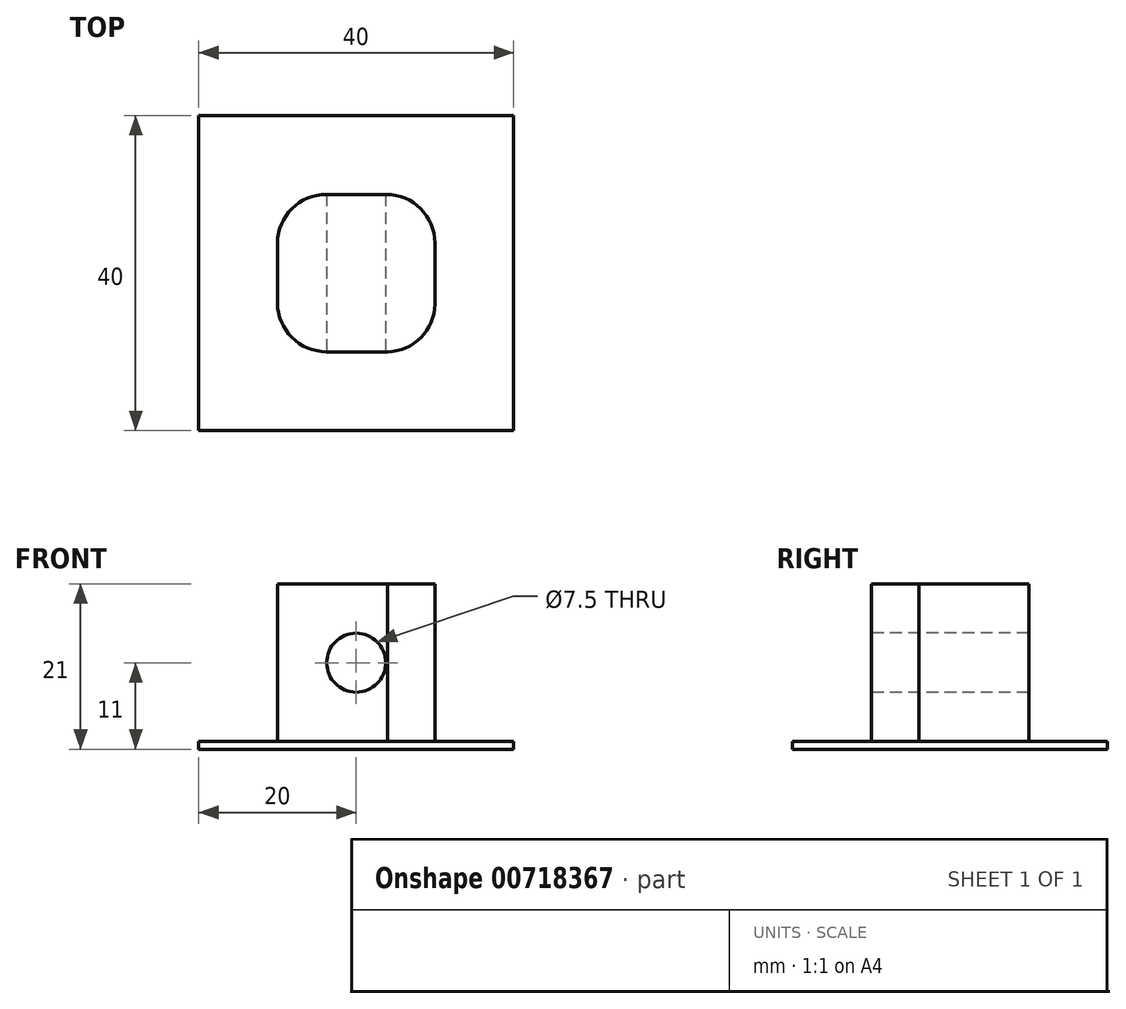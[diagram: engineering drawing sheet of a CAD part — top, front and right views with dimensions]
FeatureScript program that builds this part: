
annotation { "Feature Type Name" : "Feature", "Feature Type Description" : "" }
export const myFeature = defineFeature(function(context is Context, id is Id, definition is map)
    precondition{}
    {
        {
            var Q0;
            Q0=qCreatedBy(makeId("Top.planeOp"),FACE);
            var sketch = newSketch(context, id + "F0", { "sketchPlane" : qUnion([Q0])});
            skLineSegment(sketch, "E0.bottom", {"start": v(20, -20) * mm, "end": v(-20, -20) * mm});
            skLineSegment(sketch, "E0.top", {"start": v(20, 20) * mm, "end": v(-20, 20) * mm});
            skLineSegment(sketch, "E0.left", {"start": v(20, -20) * mm, "end": v(20, 20) * mm});
            skLineSegment(sketch, "E0.right", {"start": v(-20, -20) * mm, "end": v(-20, 20) * mm});
            skPoint(sketch, "E0.middle", {"position": v(0, 0) * mm});
            skSolve(sketch);
        }
        {
            var Q0;
            Q0=makeQuery(id+"F0.imprint","IMPRINT",FACE,{"disambiguationData":[TD([[makeQuery(id+"F0.imprint","IMPRINT",EDGE,{"derivedFrom":sQuery(id+"F0.wireOp",EDGE,"E0.bottom")}),-1.0]])]});
            extrude(context, id + "F1", {"entities" : qUnion([Q0]), "depth" : 1 * mm, "offsetDistance" : 25 * mm});
        }
        {
            var Q0;
            Q0=makeQuery(id+"F1.opExtrude","CAP_FACE",FACE,{"disambiguationData":[OSD([sQuery(id+"F0.wireOp",EDGE,"E0.bottom"),sQuery(id+"F0.wireOp",EDGE,"E0.top"),sQuery(id+"F0.wireOp",EDGE,"E0.left"),sQuery(id+"F0.wireOp",EDGE,"E0.right")])],"isStart":false});
            var sketch = newSketch(context, id + "F2", { "sketchPlane" : qUnion([Q0])});
            skLineSegment(sketch, "E1.bottom", {"start": v(10, -10) * mm, "end": v(-10, -10) * mm});
            skLineSegment(sketch, "E1.top", {"start": v(10, 10) * mm, "end": v(-10, 10) * mm});
            skLineSegment(sketch, "E1.left", {"start": v(10, -10) * mm, "end": v(10, 10) * mm});
            skLineSegment(sketch, "E1.right", {"start": v(-10, -10) * mm, "end": v(-10, 10) * mm});
            skPoint(sketch, "E1.middle", {"position": v(0, 0) * mm});
            skSolve(sketch);
        }
        {
            var Q0;
            Q0=makeQuery(id+"F2.imprint","IMPRINT",FACE,{"disambiguationData":[TD([[makeQuery(id+"F2.imprint","IMPRINT",EDGE,{"derivedFrom":sQuery(id+"F2.wireOp",EDGE,"E1.bottom")}),-1.0]])]});
            extrude(context, id + "F3", {"entities" : qUnion([Q0]), "operationType" : NewBodyOperationType.ADD, "depth" : 20 * mm, "offsetDistance" : 25 * mm});
        }
        {
            var Q0;
            Q0=makeQuery(id+"F3.opExtrude","SWEPT_FACE",FACE,{"disambiguationData":[OSD([sQuery(id+"F2.wireOp",EDGE,"E1.bottom")])]});
            var sketch = newSketch(context, id + "F4", { "sketchPlane" : qUnion([Q0])});
            skCircle(sketch, "E2", {"center": v(0, 11) * mm, "radius": 3.75 * mm});
            skSolve(sketch);
        }
        {
            var Q0;
            Q0=makeQuery(id+"F3.opExtrude","CAP_FACE",FACE,{"disambiguationData":[OSD([sQuery(id+"F2.wireOp",EDGE,"E1.bottom"),sQuery(id+"F2.wireOp",EDGE,"E1.top"),sQuery(id+"F2.wireOp",EDGE,"E1.left"),sQuery(id+"F2.wireOp",EDGE,"E1.right")])],"isStart":false});
            var sketch = newSketch(context, id + "F5", { "sketchPlane" : qUnion([Q0])});
            skLineSegment(sketch, "E3", {"start": v(3.75, 0) * mm, "end": v(3.75, -10) * mm});
            skLineSegment(sketch, "E4", {"start": v(3.75, 0) * mm, "end": v(3.75, 10) * mm});
            skLineSegment(sketch, "E5", {"start": v(-3.75, 0) * mm, "end": v(-3.75, -10) * mm});
            skLineSegment(sketch, "E6", {"start": v(-3.75, -10) * mm, "end": v(-3.75, 10) * mm});
            skLineSegment(sketch, "E7", {"start": v(0, 3.75) * mm, "end": v(10, 3.75) * mm});
            skLineSegment(sketch, "E8", {"start": v(10, 3.75) * mm, "end": v(0, 3.75) * mm});
            skLineSegment(sketch, "E9", {"start": v(-10, 3.75) * mm, "end": v(0, 3.75) * mm});
            skLineSegment(sketch, "E10", {"start": v(0, -3.75) * mm, "end": v(-10, -3.75) * mm});
            skLineSegment(sketch, "E11", {"start": v(-10, -3.75) * mm, "end": v(10, -3.75) * mm});
            skArc(sketch, "E12", {"start": v(3.75, -10) * mm, "mid": v(8.2, -8.2) * mm, "end": v(10, -3.75) * mm});
            skArc(sketch, "E13", {"start": v(10, 3.75) * mm, "mid": v(8.18, 8.18) * mm, "end": v(3.75, 10) * mm});
            skArc(sketch, "E14", {"start": v(-3.75, 10) * mm, "mid": v(-8.18, 8.18) * mm, "end": v(-10, 3.75) * mm});
            skArc(sketch, "E15", {"start": v(-10, -3.75) * mm, "mid": v(-8.18, -8.18) * mm, "end": v(-3.75, -10) * mm});
            skSolve(sketch);
        }
        {
            var Q0;
            Q0=makeQuery(id+"F4.imprint","IMPRINT",FACE,{"disambiguationData":[TD([[makeQuery(id+"F4.imprint","IMPRINT",EDGE,{"derivedFrom":sQuery(id+"F4.wireOp",EDGE,"E2")}),1.0]])]});
            extrude(context, id + "F6", {"entities" : qUnion([Q0]), "operationType" : NewBodyOperationType.REMOVE, "oppositeDirection" : true, "depth" : 20 * mm, "offsetDistance" : 25 * mm});
        }
        {
            var Q0;
            {var subQ0=sQuery(id+"F5.wireOp",EDGE,"E15");var subQ1=makeQuery(id+"F3.opExtrude","CAP_EDGE",EDGE,{"disambiguationData":[OSD([sQuery(id+"F2.wireOp",EDGE,"E1.right")])],"isStart":false});var subQ2=makeQuery(id+"F5.imprint","INTERSECT",VERTEX,{"derivedFrom":[subQ1,subQ0]});var subQ3=makeQuery(id+"F3.opExtrude","CAP_EDGE",EDGE,{"disambiguationData":[OSD([sQuery(id+"F2.wireOp",EDGE,"E1.bottom")])],"isStart":false});var subQ4=makeQuery(id+"F5.imprint","INTERSECT",VERTEX,{"derivedFrom":[subQ3,subQ0]});Q0=makeQuery(id+"F5.imprint","IMPRINT",FACE,{"disambiguationData":[TD([[makeQuery(id+"F5.imprint","IMPRINT",EDGE,{"disambiguationData":[TD([[subQ2,-1.0],[subQ4,1.0]])],"derivedFrom":subQ0}),-1.0]])]});}
            var Q1;
            {var subQ0=sQuery(id+"F5.wireOp",EDGE,"E12");var subQ1=makeQuery(id+"F3.opExtrude","CAP_EDGE",EDGE,{"disambiguationData":[OSD([sQuery(id+"F2.wireOp",EDGE,"E1.bottom")])],"isStart":false});var subQ2=makeQuery(id+"F5.imprint","INTERSECT",VERTEX,{"derivedFrom":[subQ1,subQ0]});Q1=makeQuery(id+"F5.imprint","IMPRINT",FACE,{"disambiguationData":[TD([[makeQuery(id+"F5.imprint","IMPRINT",EDGE,{"disambiguationData":[TD([[subQ2,-1.0]])],"derivedFrom":subQ0}),-1.0]])]});}
            var Q2;
            {var subQ0=sQuery(id+"F5.wireOp",EDGE,"E13");var subQ1=makeQuery(id+"F3.opExtrude","CAP_EDGE",EDGE,{"disambiguationData":[OSD([sQuery(id+"F2.wireOp",EDGE,"E1.top")])],"isStart":false});var subQ2=makeQuery(id+"F5.imprint","INTERSECT",VERTEX,{"derivedFrom":[subQ1,subQ0]});Q2=makeQuery(id+"F5.imprint","IMPRINT",FACE,{"disambiguationData":[TD([[makeQuery(id+"F5.imprint","IMPRINT",EDGE,{"disambiguationData":[TD([[subQ2,1.0]])],"derivedFrom":subQ0}),-1.0]])]});}
            var Q3;
            {var subQ0=sQuery(id+"F5.wireOp",EDGE,"E14");var subQ3=makeQuery(id+"F3.opExtrude","CAP_EDGE",EDGE,{"disambiguationData":[OSD([sQuery(id+"F2.wireOp",EDGE,"E1.top")])],"isStart":false});var subQ4=makeQuery(id+"F5.imprint","INTERSECT",VERTEX,{"derivedFrom":[subQ3,subQ0]});Q3=makeQuery(id+"F5.imprint","IMPRINT",FACE,{"disambiguationData":[TD([[makeQuery(id+"F5.imprint","IMPRINT",EDGE,{"disambiguationData":[TD([[subQ4,-1.0]])],"derivedFrom":subQ0}),-1.0]])]});}
            extrude(context, id + "F7", {"entities" : qUnion([Q0, Q1, Q2, Q3]), "operationType" : NewBodyOperationType.REMOVE, "oppositeDirection" : true, "depth" : 20 * mm, "offsetDistance" : 25 * mm});
        }
    });
